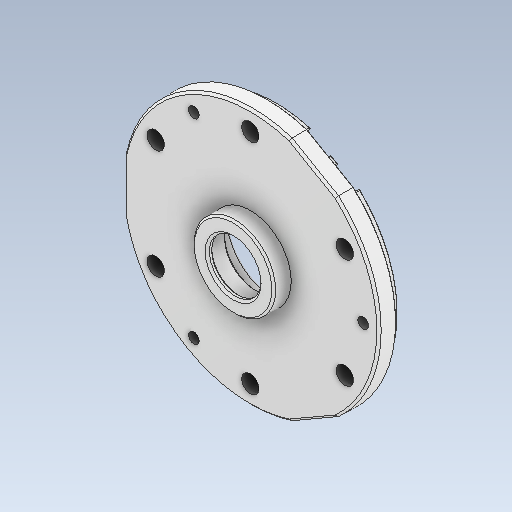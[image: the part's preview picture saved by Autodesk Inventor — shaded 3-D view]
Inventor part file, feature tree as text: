
AUTODESK INVENTOR PART (.ipt)
format: ipt  version: 2020 (Build 240168000, 168)  size: 1,246,720 bytes
history: native  units: in
note: dims shown in document units (in); Inventor stores cm internally (conversion verified against a paired STEP export)
features: chamfer x1
ambient origin geometry x8: Origin, YZ Plane, XZ Plane, XY Plane, X Axis, Y Axis, Z Axis, Center Point
bodies: Solid1 (feature_tree)
feature tree (1):
  chamfer  "Chamfer3"  [1 undecoded]
note: 1 required parameter value undecoded (feature->parameter linkage not recoverable at this tier; creation-order binding heuristic only, values carry confidence <= 0.55)
